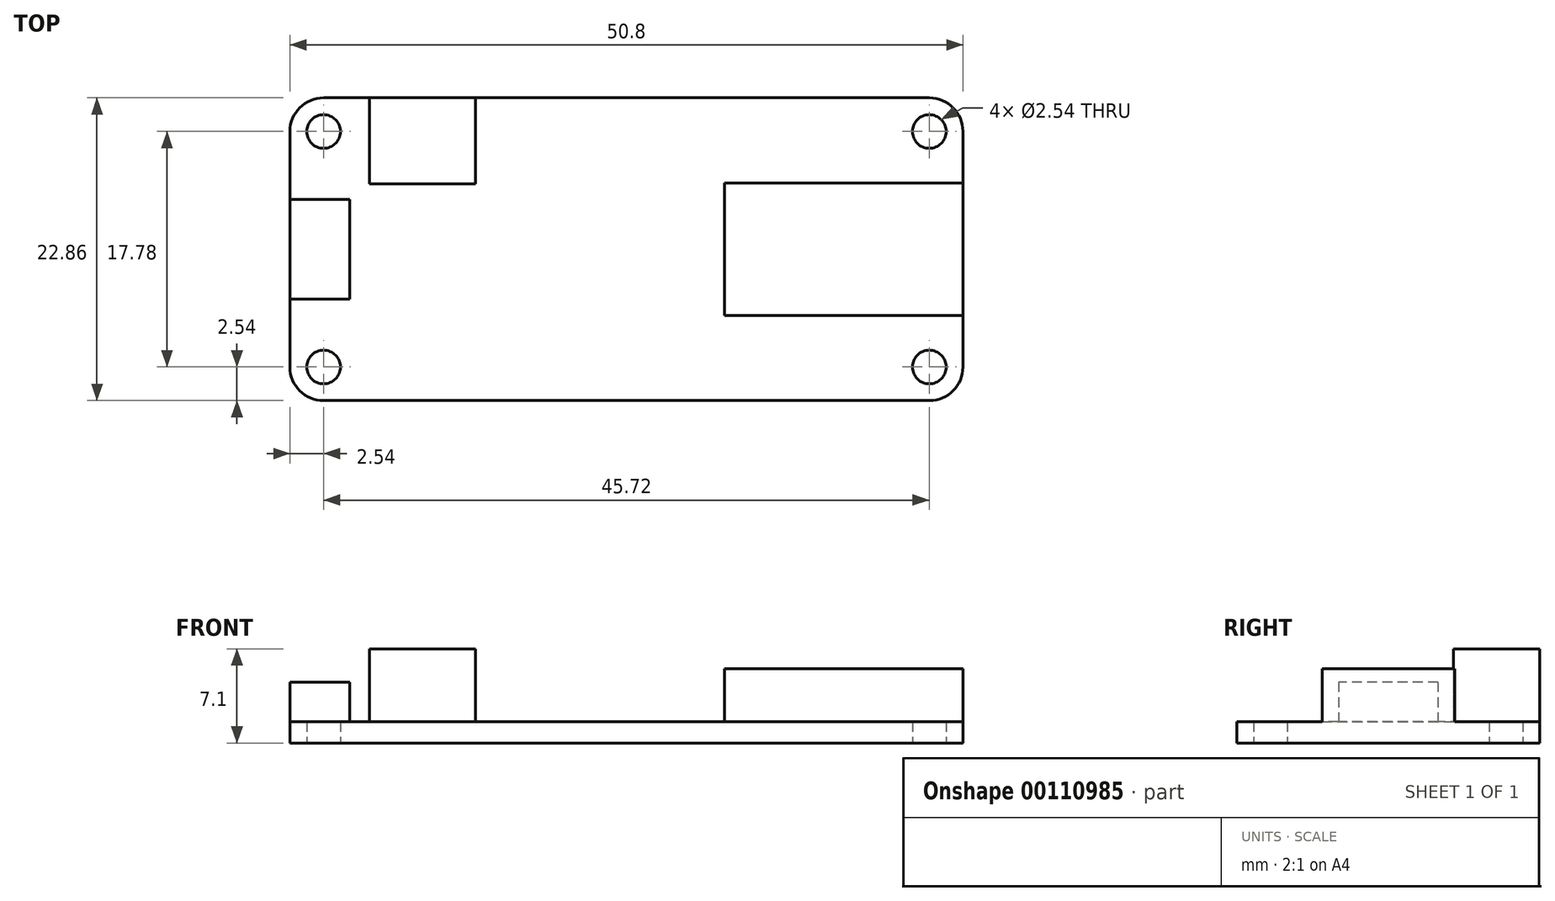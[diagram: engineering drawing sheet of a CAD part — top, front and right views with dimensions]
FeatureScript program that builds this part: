
annotation { "Feature Type Name" : "Feature", "Feature Type Description" : "" }
export const myFeature = defineFeature(function(context is Context, id is Id, definition is map)
    precondition{}
    {
        {
            var Q0;
            Q0=qCreatedBy(makeId("Top.planeOp"),FACE);
            var sketch = newSketch(context, id + "F0", { "sketchPlane" : qUnion([Q0])});
            skLineSegment(sketch, "E0.bottom", {"start": v(22.86, 11.43) * mm, "end": v(-22.86, 11.43) * mm});
            skLineSegment(sketch, "E0.top", {"start": v(22.86, -11.43) * mm, "end": v(-22.86, -11.43) * mm});
            skLineSegment(sketch, "E0.left", {"start": v(25.4, 8.9) * mm, "end": v(25.4, -8.9) * mm});
            skLineSegment(sketch, "E0.right", {"start": v(-25.4, 8.9) * mm, "end": v(-25.4, -8.9) * mm});
            skPoint(sketch, "E0.middle", {"position": v(0, 0) * mm});
            skCircle(sketch, "E1", {"center": v(-22.86, 8.89) * mm, "radius": 1.27 * mm});
            skCircle(sketch, "E2", {"center": v(22.86, 8.89) * mm, "radius": 1.27 * mm});
            skCircle(sketch, "E3", {"center": v(-22.86, -8.89) * mm, "radius": 1.27 * mm});
            skCircle(sketch, "E4", {"center": v(22.86, -8.89) * mm, "radius": 1.27 * mm});
            skPoint(sketch, "E5.visualSharp", {"position": v(-25.4, 11.43) * mm});
            skArc(sketch, "E5.filletArc", {"start": v(-22.86, 11.43) * mm, "mid": v(-24.66, 10.69) * mm, "end": v(-25.4, 8.9) * mm});
            skPoint(sketch, "E6.visualSharp", {"position": v(-25.4, -11.43) * mm});
            skArc(sketch, "E6.filletArc", {"start": v(-25.4, -8.9) * mm, "mid": v(-24.66, -10.69) * mm, "end": v(-22.86, -11.43) * mm});
            skPoint(sketch, "E7.visualSharp", {"position": v(25.4, -11.43) * mm});
            skArc(sketch, "E7.filletArc", {"start": v(22.86, -11.43) * mm, "mid": v(24.66, -10.69) * mm, "end": v(25.4, -8.9) * mm});
            skPoint(sketch, "E8.visualSharp", {"position": v(25.4, 11.43) * mm});
            skArc(sketch, "E8.filletArc", {"start": v(25.4, 8.9) * mm, "mid": v(24.66, 10.69) * mm, "end": v(22.86, 11.43) * mm});
            skSolve(sketch);
        }
        {
            var Q0;
            Q0 = qSketchRegion(id + "F0", true);
            extrude(context, id + "F1", {"entities" : qUnion([Q0]), "depth" : 1.6 * mm});
        }
        {
            var Q0;
            Q0=makeQuery(id+"F1.opExtrude","CAP_FACE",FACE,{"disambiguationData":[OSD([sQuery(id+"F0.wireOp",EDGE,"E0.bottom"),sQuery(id+"F0.wireOp",EDGE,"E0.top"),sQuery(id+"F0.wireOp",EDGE,"E0.left"),sQuery(id+"F0.wireOp",EDGE,"E0.right"),sQuery(id+"F0.wireOp",EDGE,"E1"),sQuery(id+"F0.wireOp",EDGE,"E2"),sQuery(id+"F0.wireOp",EDGE,"E3"),sQuery(id+"F0.wireOp",EDGE,"E4"),sQuery(id+"F0.wireOp",EDGE,"E5.filletArc"),sQuery(id+"F0.wireOp",EDGE,"E6.filletArc"),sQuery(id+"F0.wireOp",EDGE,"E7.filletArc"),sQuery(id+"F0.wireOp",EDGE,"E8.filletArc")])],"isStart":false});
            var sketch = newSketch(context, id + "F2", { "sketchPlane" : qUnion([Q0])});
            skLineSegment(sketch, "E9.bottom", {"start": v(-25.4, 3.75) * mm, "end": v(-20.9, 3.75) * mm});
            skLineSegment(sketch, "E9.top", {"start": v(-25.4, -3.75) * mm, "end": v(-20.9, -3.75) * mm});
            skLineSegment(sketch, "E9.left", {"start": v(-25.4, 3.75) * mm, "end": v(-25.4, -3.75) * mm});
            skLineSegment(sketch, "E9.right", {"start": v(-20.9, 3.75) * mm, "end": v(-20.9, -3.75) * mm});
            skPoint(sketch, "E9.middle", {"position": v(-23.15, 0) * mm});
            skSolve(sketch);
        }
        {
            var Q0;
            Q0 = qSketchRegion(id + "F2", true);
            extrude(context, id + "F3", {"entities" : qUnion([Q0]), "operationType" : NewBodyOperationType.ADD, "depth" : 3 * mm});
        }
        {
            var Q0;
            Q0=makeQuery(id+"F1.opExtrude","CAP_FACE",FACE,{"disambiguationData":[OSD([sQuery(id+"F0.wireOp",EDGE,"E0.bottom"),sQuery(id+"F0.wireOp",EDGE,"E0.top"),sQuery(id+"F0.wireOp",EDGE,"E0.left"),sQuery(id+"F0.wireOp",EDGE,"E0.right"),sQuery(id+"F0.wireOp",EDGE,"E1"),sQuery(id+"F0.wireOp",EDGE,"E2"),sQuery(id+"F0.wireOp",EDGE,"E3"),sQuery(id+"F0.wireOp",EDGE,"E4"),sQuery(id+"F0.wireOp",EDGE,"E5.filletArc"),sQuery(id+"F0.wireOp",EDGE,"E6.filletArc"),sQuery(id+"F0.wireOp",EDGE,"E7.filletArc"),sQuery(id+"F0.wireOp",EDGE,"E8.filletArc")])],"isStart":false});
            var sketch = newSketch(context, id + "F4", { "sketchPlane" : qUnion([Q0])});
            skLineSegment(sketch, "E10.bottom", {"start": v(25.4, -5) * mm, "end": v(7.4, -5) * mm});
            skLineSegment(sketch, "E10.top", {"start": v(25.4, 5) * mm, "end": v(7.4, 5) * mm});
            skLineSegment(sketch, "E10.left", {"start": v(25.4, -5) * mm, "end": v(25.4, 5) * mm});
            skLineSegment(sketch, "E10.right", {"start": v(7.4, -5) * mm, "end": v(7.4, 5) * mm});
            skPoint(sketch, "E10.middle", {"position": v(16.4, 0) * mm});
            skSolve(sketch);
        }
        {
            var Q0;
            Q0=makeQuery(id+"F4.imprint","IMPRINT",FACE,{"disambiguationData":[TD([[makeQuery(id+"F4.imprint","IMPRINT",EDGE,{"derivedFrom":sQuery(id+"F4.wireOp",EDGE,"E10.bottom")}),-1.0]])]});
            extrude(context, id + "F5", {"entities" : qUnion([Q0]), "operationType" : NewBodyOperationType.ADD, "depth" : 4 * mm});
        }
        {
            var Q0;
            Q0=makeQuery(id+"F1.opExtrude","CAP_FACE",FACE,{"disambiguationData":[OSD([sQuery(id+"F0.wireOp",EDGE,"E0.bottom"),sQuery(id+"F0.wireOp",EDGE,"E0.top"),sQuery(id+"F0.wireOp",EDGE,"E0.left"),sQuery(id+"F0.wireOp",EDGE,"E0.right"),sQuery(id+"F0.wireOp",EDGE,"E1"),sQuery(id+"F0.wireOp",EDGE,"E2"),sQuery(id+"F0.wireOp",EDGE,"E3"),sQuery(id+"F0.wireOp",EDGE,"E4"),sQuery(id+"F0.wireOp",EDGE,"E5.filletArc"),sQuery(id+"F0.wireOp",EDGE,"E6.filletArc"),sQuery(id+"F0.wireOp",EDGE,"E7.filletArc"),sQuery(id+"F0.wireOp",EDGE,"E8.filletArc")])],"isStart":false});
            var sketch = newSketch(context, id + "F6", { "sketchPlane" : qUnion([Q0])});
            skLineSegment(sketch, "E11.bottom", {"start": v(-19.4, 11.43) * mm, "end": v(-11.4, 11.43) * mm});
            skLineSegment(sketch, "E11.top", {"start": v(-19.4, 4.93) * mm, "end": v(-11.4, 4.93) * mm});
            skLineSegment(sketch, "E11.left", {"start": v(-19.4, 11.43) * mm, "end": v(-19.4, 4.93) * mm});
            skLineSegment(sketch, "E11.right", {"start": v(-11.4, 11.43) * mm, "end": v(-11.4, 4.93) * mm});
            skSolve(sketch);
        }
        {
            var Q0;
            Q0=makeQuery(id+"F6.imprint","IMPRINT",FACE,{"disambiguationData":[TD([[makeQuery(id+"F6.imprint","IMPRINT",EDGE,{"derivedFrom":sQuery(id+"F6.wireOp",EDGE,"E11.bottom")}),1.0]])]});
            extrude(context, id + "F7", {"entities" : qUnion([Q0]), "operationType" : NewBodyOperationType.ADD, "depth" : 5.5 * mm});
        }
    });
